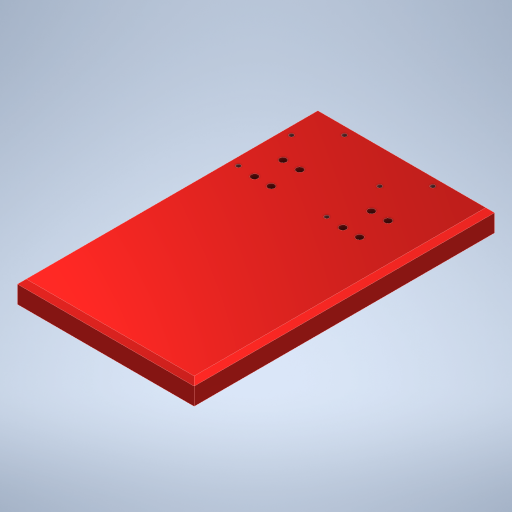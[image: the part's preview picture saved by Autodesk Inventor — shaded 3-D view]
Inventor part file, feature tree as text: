
AUTODESK INVENTOR PART (.ipt)
format: ipt  version: 2023 (Build 270158000, 158)  size: 280,064 bytes
history: native  units: in
note: dims shown in document units (in); Inventor stores cm internally (conversion verified against a paired STEP export)
features: sketch x3, extrude x2, hole x1, chamfer x1
ambient origin geometry x8: Origin, YZ Plane, XZ Plane, XY Plane, X Axis, Y Axis, Z Axis, Center Point
bodies: Solid1 (feature_tree)
feature tree (7):
  extrude  "Extrusion1"  Depth=5.0in
  hole  "Hole1"  [1 undecoded]
  extrude  "Extrusion2"  Depth=0.3937in
  chamfer  "Chamfer1"  Distance=0.75in
  sketch  "Sketch1"  dims[d0=8.5in d1=5.0in]
  sketch  "Sketch2"  dims[d2=0.6201in d3=0.0in d4=0.35in]
  sketch  "Sketch3"  dims[d5=0.35in d7=0.75in d8=0.75in d9=0.1276in d10=0.315in d11=0.4in d12=0.61in d13=0.5635in d14=1.0in d15=0.8108in d16=1.5in d17=0.1969in d18=0.1969in d19=0.1969in d20=0.1969in d21=0.807in d22=0.472in d23=0.842in d24=1.826in d25=0.0in d26=0.0in d27=0.7874in d29=2.5in d30=0.3937in d32=1.0in d34=0.7874in d36=2.5in d37=0.3937in d39=1.0in d41=0.125in d42=0.125in d43=45.0deg]
note: 1 required parameter value undecoded (feature->parameter linkage not recoverable at this tier; creation-order binding heuristic only, values carry confidence <= 0.55)
